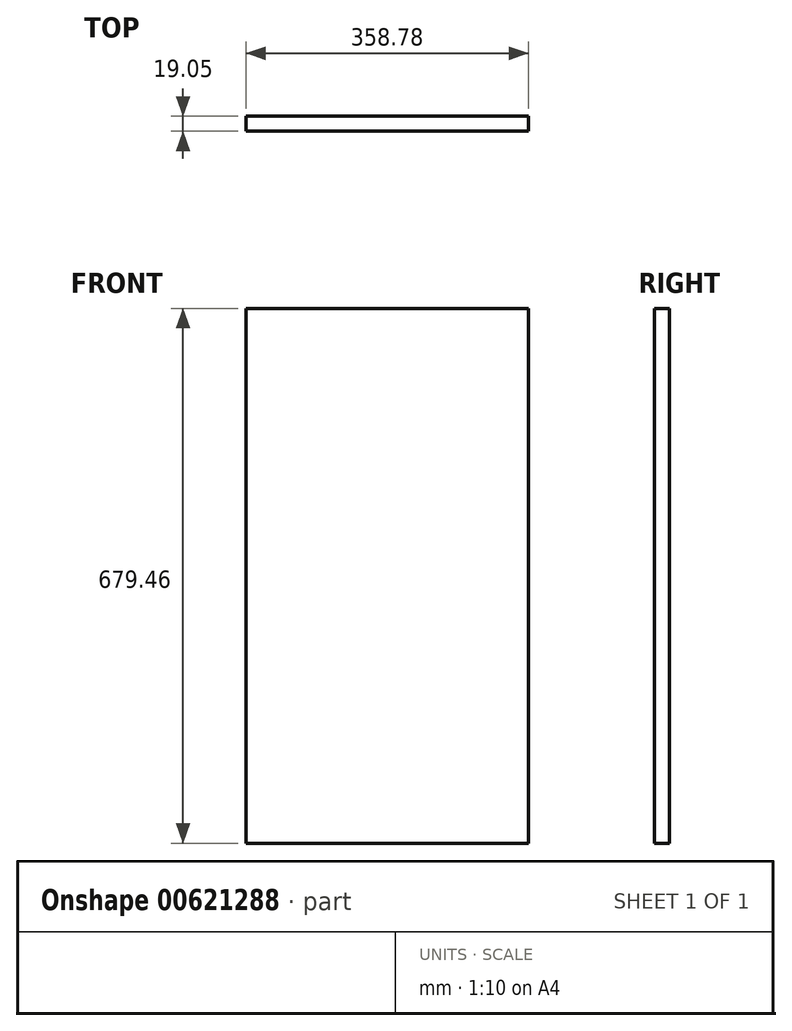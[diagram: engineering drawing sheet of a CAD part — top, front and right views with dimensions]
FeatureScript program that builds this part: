
annotation { "Feature Type Name" : "Feature", "Feature Type Description" : "" }
export const myFeature = defineFeature(function(context is Context, id is Id, definition is map)
    precondition{}
    {
        {
            var Q0;
            Q0=qCreatedBy(makeId("Front.planeOp"),FACE);
            var sketch = newSketch(context, id + "F0", { "sketchPlane" : qUnion([Q0])});
            skLineSegment(sketch, "E0.bottom", {"start": v(179.39, 339.73) * mm, "end": v(-179.39, 339.73) * mm});
            skLineSegment(sketch, "E0.top", {"start": v(179.39, -339.73) * mm, "end": v(-179.39, -339.73) * mm});
            skLineSegment(sketch, "E0.left", {"start": v(179.39, 339.73) * mm, "end": v(179.39, -339.73) * mm});
            skLineSegment(sketch, "E0.right", {"start": v(-179.39, 339.73) * mm, "end": v(-179.39, -339.73) * mm});
            skPoint(sketch, "E0.middle", {"position": v(0, 0) * mm});
            skSolve(sketch);
        }
        {
            var Q0;
            Q0=makeQuery(id+"F0.imprint","IMPRINT",FACE,{"disambiguationData":[TD([[makeQuery(id+"F0.imprint","IMPRINT",EDGE,{"derivedFrom":sQuery(id+"F0.wireOp",EDGE,"E0.bottom")}),1.0]])]});
            extrude(context, id + "F1", {"entities" : qUnion([Q0]), "depth" : 19.05 * mm, "offsetDistance" : 25.4 * mm});
        }
    });
